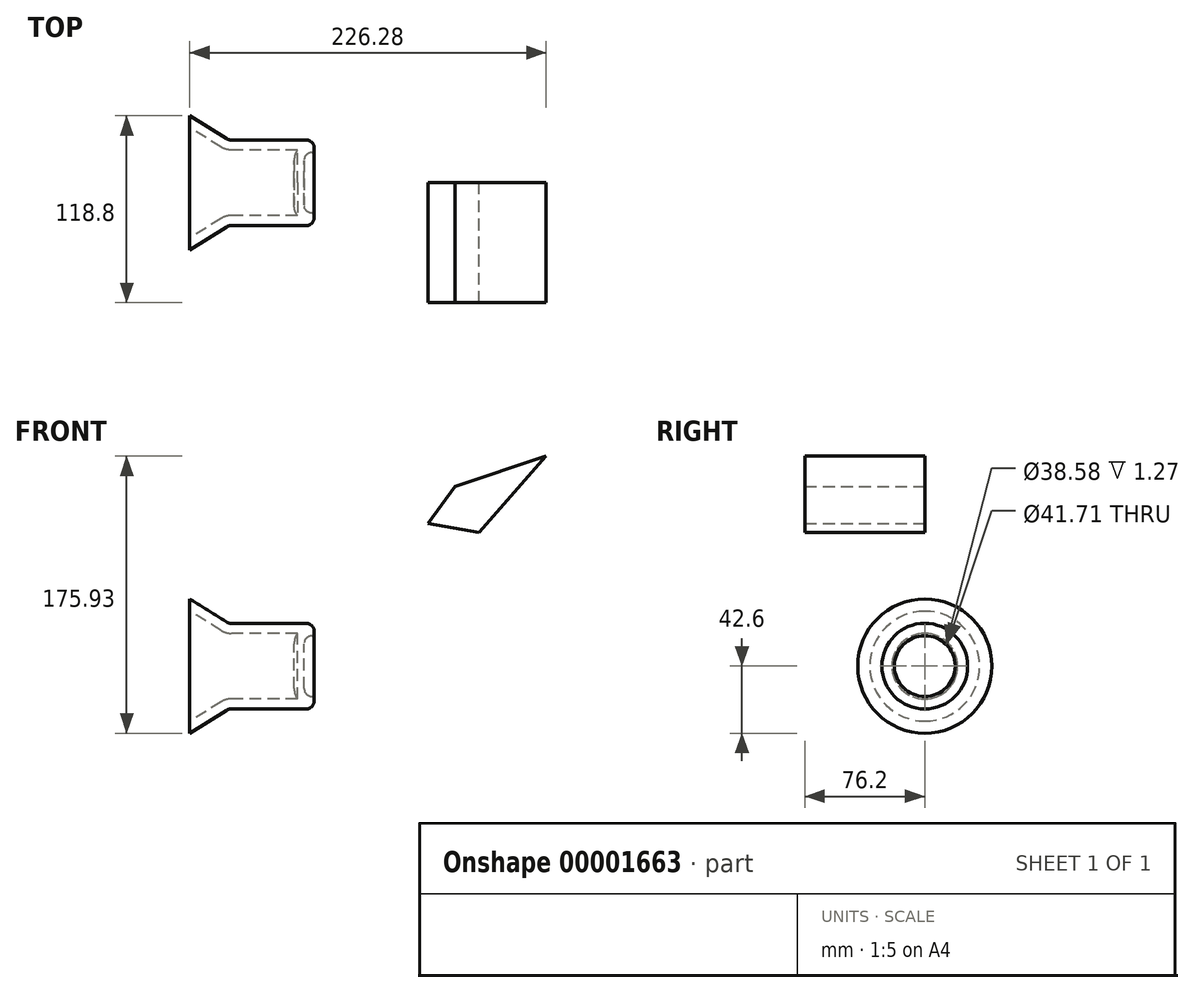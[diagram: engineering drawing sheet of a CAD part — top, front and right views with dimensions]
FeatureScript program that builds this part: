
annotation { "Feature Type Name" : "Feature", "Feature Type Description" : "" }
export const myFeature = defineFeature(function(context is Context, id is Id, definition is map)
    precondition{}
    {
        {
            var Q0;
            Q0=qCreatedBy(makeId("Front.planeOp"),FACE);
            var sketch = newSketch(context, id + "F0", { "sketchPlane" : qUnion([Q0])});
            skLineSegment(sketch, "E0", {"start": v(0, 0) * mm, "end": v(0, 27.2) * mm});
            skLineSegment(sketch, "E1", {"start": v(0, 27.2) * mm, "end": v(-54.35, 27.2) * mm});
            skLineSegment(sketch, "E2", {"start": v(-54.35, 27.2) * mm, "end": v(-79.03, 42.6) * mm});
            skLineSegment(sketch, "E3", {"start": v(-79.03, 42.6) * mm, "end": v(-77.07, 0) * mm});
            skLineSegment(sketch, "E4", {"start": v(-77.07, 0) * mm, "end": v(0, 0) * mm});
            skSolve(sketch);
        }
        {
            var Q0;
            Q0 = qSketchRegion(id + "F0", true);
            var Q1;
            Q1=sQuery(id+"F0.wireOp",EDGE,"E4");
            revolve(context, id + "F1", {"entities" : qUnion([Q0]), "axis" : qUnion([Q1]), "revolveType" : RevolveType.FULL});
        }
        {
            var Q0;
            Q0=makeQuery(id+"F1.opRevolve","SWEPT_FACE",FACE,{"disambiguationData":[OSD([sQuery(id+"F0.wireOp",EDGE,"E0")])]});
            var sketch = newSketch(context, id + "F2", { "sketchPlane" : qUnion([Q0])});
            skCircle(sketch, "E5", {"center": v(0, 0) * mm, "radius": 19.29 * mm});
            skSolve(sketch);
        }
        {
            var Q0;
            Q0 = qSketchRegion(id + "F2", true);
            extrude(context, id + "F3", {"entities" : qUnion([Q0]), "operationType" : NewBodyOperationType.REMOVE, "oppositeDirection" : true, "depth" : 6.35 * mm});
        }
        {
            var Q0;
            Q0=makeQuery(id+"F1.opRevolve","SWEPT_FACE",FACE,{"disambiguationData":[OSD([sQuery(id+"F0.wireOp",EDGE,"E1")])]});
            var Q1;
            Q1=makeQuery(id+"F3.boolean.opBoolean","COPY",FACE,{"derivedFrom":makeQuery(id+"F3.opExtrude","CAP_FACE",FACE,{"disambiguationData":[OSD([sQuery(id+"F2.wireOp",EDGE,"E5")])],"isStart":false})});
            fillet(context, id + "F4", {"entities" : qUnion([Q0, Q1]), "radius" : 5.08 * mm, "tangentPropagation" : true, "allowEdgeOverflow" : false});
        }
        {
            var Q0;
            Q0=makeQuery(id+"F1.opRevolve","SWEPT_FACE",FACE,{"disambiguationData":[OSD([sQuery(id+"F0.wireOp",EDGE,"E3")])]});
            shell(context, id + "F5", {"entities" : qUnion([Q0]), "thickness" : 6.35 * mm});
        }
        {
            var Q0;
            Q0=qCreatedBy(makeId("Front.planeOp"),FACE);
            var sketch = newSketch(context, id + "F6", { "sketchPlane" : qUnion([Q0])});
            skLineSegment(sketch, "E6", {"start": v(30.36, 146.5) * mm, "end": v(30.36, 111.07) * mm});
            skLineSegment(sketch, "E7", {"start": v(30.36, 111.07) * mm, "end": v(63.49, 111.07) * mm});
            skLineSegment(sketch, "E8", {"start": v(63.49, 111.07) * mm, "end": v(63.49, 146.38) * mm});
            skLineSegment(sketch, "E9", {"start": v(63.49, 146.38) * mm, "end": v(30.36, 146.5) * mm});
            skSolve(sketch);
        }
        {
            var Q0;
            Q0=qCreatedBy(makeId("Front.planeOp"),FACE);
            var sketch = newSketch(context, id + "F7", { "sketchPlane" : qUnion([Q0])});
            skLineSegment(sketch, "E10", {"start": v(72.42, 90.51) * mm, "end": v(104.81, 84.97) * mm});
            skLineSegment(sketch, "E11", {"start": v(104.81, 84.97) * mm, "end": v(147.25, 133.33) * mm});
            skLineSegment(sketch, "E12", {"start": v(147.25, 133.33) * mm, "end": v(89.55, 114.07) * mm});
            skLineSegment(sketch, "E13", {"start": v(89.55, 114.07) * mm, "end": v(72.42, 90.51) * mm});
            skSolve(sketch);
        }
        {
            var Q0;
            Q0 = qSketchRegion(id + "F7", true);
            extrude(context, id + "F8", {"entities" : qUnion([Q0]), "depth" : 76.2 * mm});
        }
    });
